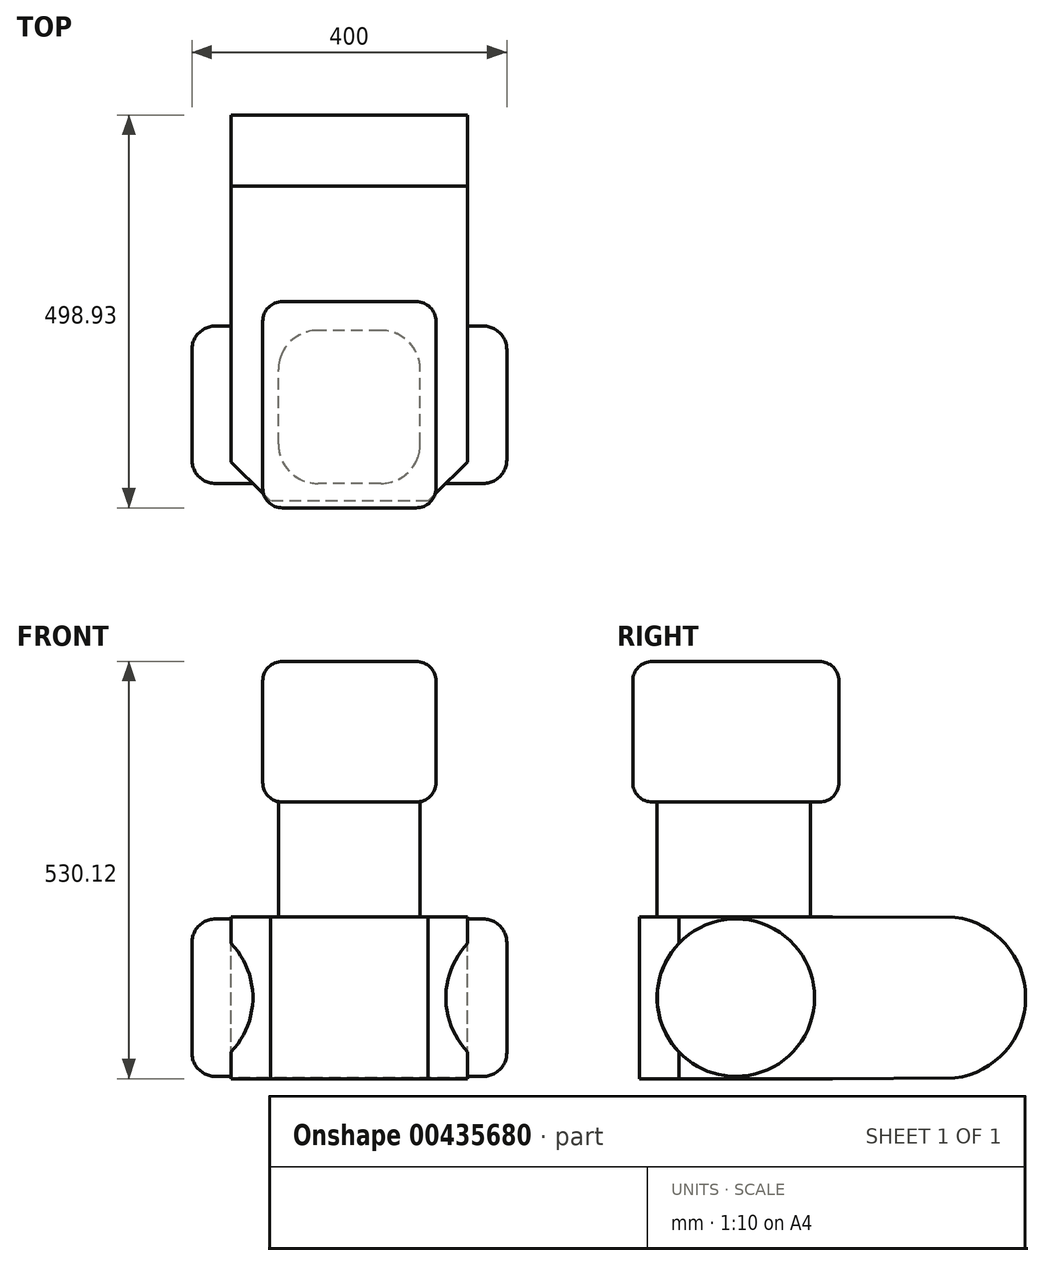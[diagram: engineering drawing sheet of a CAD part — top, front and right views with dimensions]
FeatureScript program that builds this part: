
annotation { "Feature Type Name" : "Feature", "Feature Type Description" : "" }
export const myFeature = defineFeature(function(context is Context, id is Id, definition is map)
    precondition{}
    {
        {
            var Q0;
            Q0=qCreatedBy(makeId("Right.planeOp"),FACE);
            var sketch = newSketch(context, id + "F0", { "sketchPlane" : qUnion([Q0])});
            skCircle(sketch, "E0", {"center": v(0, 0) * mm, "radius": 100 * mm});
            skLineSegment(sketch, "E1.bottom", {"start": v(-122.44, 102.88) * mm, "end": v(122.44, 102.88) * mm});
            skLineSegment(sketch, "E1.top", {"start": v(-122.44, -102.88) * mm, "end": v(122.44, -102.88) * mm});
            skLineSegment(sketch, "E1.left", {"start": v(-122.44, 102.88) * mm, "end": v(-122.44, -102.88) * mm});
            skLineSegment(sketch, "E1.right", {"start": v(122.44, 102.88) * mm, "end": v(122.44, -102.88) * mm});
            skPoint(sketch, "E2.firstSnap0", {"position": v(-122.44, 0) * mm});
            skLineSegment(sketch, "E2.bottom", {"start": v(-100, 0) * mm, "end": v(94.56, 0) * mm});
            skLineSegment(sketch, "E2.top", {"start": v(-100, 248.46) * mm, "end": v(94.56, 248.46) * mm});
            skLineSegment(sketch, "E2.left", {"start": v(-100, 0) * mm, "end": v(-100, 248.46) * mm});
            skLineSegment(sketch, "E2.right", {"start": v(94.56, 0) * mm, "end": v(94.56, 248.46) * mm});
            skLineSegment(sketch, "E3.bottom", {"start": v(130.98, 248.46) * mm, "end": v(-130.98, 248.46) * mm});
            skLineSegment(sketch, "E3.top", {"start": v(130.98, 427.24) * mm, "end": v(-130.98, 427.24) * mm});
            skLineSegment(sketch, "E3.left", {"start": v(130.98, 248.46) * mm, "end": v(130.98, 427.24) * mm});
            skLineSegment(sketch, "E3.right", {"start": v(-130.98, 248.46) * mm, "end": v(-130.98, 427.24) * mm});
            skPoint(sketch, "E3.middle", {"position": v(0, 337.85) * mm});
            skPoint(sketch, "E3.middle.positionSnap0", {"position": v(0, -102.88) * mm});
            skPoint(sketch, "E3.centerSnap0", {"position": v(0, -102.88) * mm});
            skCircle(sketch, "E4", {"center": v(265.07, 0) * mm, "radius": 102.88 * mm});
            skPoint(sketch, "E4.centerSnap0", {"position": v(122.44, 0) * mm});
            skLineSegment(sketch, "E5", {"start": v(122.44, 102.88) * mm, "end": v(277.99, 102.07) * mm});
            skLineSegment(sketch, "E6", {"start": v(277.99, 102.07) * mm, "end": v(277.99, -102.07) * mm});
            skLineSegment(sketch, "E7", {"start": v(277.99, -102.07) * mm, "end": v(122.44, -102.88) * mm});
            skLineSegment(sketch, "E8", {"start": v(-100, 210.38) * mm, "end": v(94.56, 209.37) * mm});
            skLineSegment(sketch, "E9", {"start": v(-100, 157.41) * mm, "end": v(94.56, 157.41) * mm});
            skLineSegment(sketch, "E10", {"start": v(-130.98, 296.46) * mm, "end": v(130.98, 296.46) * mm});
            skLineSegment(sketch, "E11", {"start": v(-130.98, 337.85) * mm, "end": v(130.98, 337.85) * mm});
            skLineSegment(sketch, "E12", {"start": v(-130.98, 385.86) * mm, "end": v(130.98, 385.86) * mm});
            skSolve(sketch);
        }
        {
            var Q0;
            {var subQ5=sQuery(id+"F0.wireOp",EDGE,"E9");Q0=makeQuery(id+"F0.imprint","IMPRINT",FACE,{"disambiguationData":[TD([[makeQuery(id+"F0.imprint","IMPRINT",EDGE,{"derivedFrom":subQ5}),-1.0]])]});}
            var Q1;
            {var subQ0=sQuery(id+"F0.wireOp",EDGE,"E8");Q1=makeQuery(id+"F0.imprint","IMPRINT",FACE,{"disambiguationData":[TD([[makeQuery(id+"F0.imprint","IMPRINT",EDGE,{"derivedFrom":subQ0}),-1.0]])]});}
            var Q2;
            {var subQ3=sQuery(id+"F0.wireOp",EDGE,"E8");Q2=makeQuery(id+"F0.imprint","IMPRINT",FACE,{"disambiguationData":[TD([[makeQuery(id+"F0.imprint","IMPRINT",EDGE,{"derivedFrom":subQ3}),1.0]])]});}
            extrude(context, id + "F1", {"entities" : qUnion([Q0, Q1, Q2]), "endBound" : BoundingType.SYMMETRIC, "depth" : 180 * mm});
        }
        {
            var Q0;
            {var subQ3=sQuery(id+"F0.wireOp",EDGE,"E10");Q0=makeQuery(id+"F0.imprint","IMPRINT",FACE,{"disambiguationData":[TD([[makeQuery(id+"F0.imprint","IMPRINT",EDGE,{"derivedFrom":subQ3}),-1.0]])]});}
            var Q1;
            {var subQ0=sQuery(id+"F0.wireOp",EDGE,"E10");Q1=makeQuery(id+"F0.imprint","IMPRINT",FACE,{"disambiguationData":[TD([[makeQuery(id+"F0.imprint","IMPRINT",EDGE,{"derivedFrom":subQ0}),1.0]])]});}
            var Q2;
            {var subQ0=sQuery(id+"F0.wireOp",EDGE,"E11");Q2=makeQuery(id+"F0.imprint","IMPRINT",FACE,{"disambiguationData":[TD([[makeQuery(id+"F0.imprint","IMPRINT",EDGE,{"derivedFrom":subQ0}),1.0]])]});}
            var Q3;
            {var subQ0=sQuery(id+"F0.wireOp",EDGE,"E3.top");Q3=makeQuery(id+"F0.imprint","IMPRINT",FACE,{"disambiguationData":[TD([[makeQuery(id+"F0.imprint","IMPRINT",EDGE,{"derivedFrom":subQ0}),1.0]])]});}
            extrude(context, id + "F2", {"entities" : qUnion([Q0, Q1, Q2, Q3]), "operationType" : NewBodyOperationType.ADD, "endBound" : BoundingType.SYMMETRIC, "depth" : 220 * mm});
        }
        {
            var Q0;
            Q0=makeQuery(id+"F0.imprint","IMPRINT",FACE,{"disambiguationData":[TD([[makeQuery(id+"F0.imprint","IMPRINT",EDGE,{"derivedFrom":sQuery(id+"F0.wireOp",EDGE,"E1.top")}),1.0]])]});
            var Q1;
            {var subQ0=sQuery(id+"F0.wireOp",EDGE,"E1.right");Q1=makeQuery(id+"F0.imprint","IMPRINT",FACE,{"disambiguationData":[TD([[makeQuery(id+"F0.imprint","IMPRINT",EDGE,{"derivedFrom":subQ0}),1.0]])]});}
            var Q2;
            {var subQ5=sQuery(id+"F0.wireOp",EDGE,"E6");Q2=makeQuery(id+"F0.imprint","IMPRINT",FACE,{"disambiguationData":[TD([[makeQuery(id+"F0.imprint","IMPRINT",EDGE,{"derivedFrom":subQ5}),-1.0]])]});}
            var Q3;
            {var subQ0=sQuery(id+"F0.wireOp",EDGE,"E6");Q3=makeQuery(id+"F0.imprint","IMPRINT",FACE,{"disambiguationData":[TD([[makeQuery(id+"F0.imprint","IMPRINT",EDGE,{"derivedFrom":subQ0}),1.0]])]});}
            var Q4;
            {var subQ0=sQuery(id+"F0.wireOp",EDGE,"E2.left");var subQ5=sQuery(id+"F0.wireOp",EDGE,"E1.bottom");var subQ6=makeQuery(id+"F0.imprint","INTERSECT",VERTEX,{"derivedFrom":[subQ5,subQ0]});Q4=makeQuery(id+"F0.imprint","IMPRINT",FACE,{"disambiguationData":[TD([[makeQuery(id+"F0.imprint","IMPRINT",EDGE,{"disambiguationData":[TD([[subQ6,-1.0]])],"derivedFrom":subQ5}),-1.0]])]});}
            extrude(context, id + "F3", {"entities" : qUnion([Q0, Q1, Q2, Q3, Q4]), "operationType" : NewBodyOperationType.ADD, "endBound" : BoundingType.SYMMETRIC, "depth" : 300 * mm});
        }
        {
            var Q0;
            {var subQ0=sQuery(id+"F0.wireOp",EDGE,"E2.bottom");Q0=makeQuery(id+"F0.imprint","IMPRINT",FACE,{"disambiguationData":[TD([[makeQuery(id+"F0.imprint","IMPRINT",EDGE,{"derivedFrom":subQ0}),1.0]])]});}
            var Q1;
            {var subQ0=sQuery(id+"F0.wireOp",EDGE,"E2.bottom");Q1=makeQuery(id+"F0.imprint","IMPRINT",FACE,{"disambiguationData":[TD([[makeQuery(id+"F0.imprint","IMPRINT",EDGE,{"derivedFrom":subQ0}),-1.0]])]});}
            extrude(context, id + "F4", {"entities" : qUnion([Q0, Q1]), "operationType" : NewBodyOperationType.ADD, "endBound" : BoundingType.SYMMETRIC, "depth" : 400 * mm});
        }
        {
            var Q0;
            Q0=makeQuery(id+"F2.opExtrude","SWEPT_EDGE",EDGE,{"disambiguationData":[OSD([sQuery(id+"F0.wireOp",EDGE,"E3.top"),sQuery(id+"F0.wireOp",EDGE,"E3.right")])]});
            var Q1;
            Q1=makeQuery(id+"F2.opExtrude","CAP_EDGE",EDGE,{"disambiguationData":[OSD([sQuery(id+"F0.wireOp",EDGE,"E3.top")])],"isStart":false});
            var Q2;
            Q2=makeQuery(id+"F2.opExtrude","SWEPT_EDGE",EDGE,{"disambiguationData":[OSD([sQuery(id+"F0.wireOp",EDGE,"E3.top"),sQuery(id+"F0.wireOp",EDGE,"E3.left")])]});
            var Q3;
            Q3=makeQuery(id+"F2.opExtrude","CAP_EDGE",EDGE,{"disambiguationData":[OSD([sQuery(id+"F0.wireOp",EDGE,"E3.top")])],"isStart":true});
            var Q4;
            Q4=makeQuery(id+"F2.opExtrude","CAP_EDGE",EDGE,{"disambiguationData":[OSD([sQuery(id+"F0.wireOp",EDGE,"E3.right")])],"isStart":false});
            var Q5;
            Q5=makeQuery(id+"F2.opExtrude","CAP_EDGE",EDGE,{"disambiguationData":[OSD([sQuery(id+"F0.wireOp",EDGE,"E3.bottom")])],"isStart":false});
            var Q6;
            Q6=makeQuery(id+"F2.opExtrude","CAP_FACE",FACE,{"disambiguationData":[OSD([sQuery(id+"F0.wireOp",EDGE,"E3.bottom"),sQuery(id+"F0.wireOp",EDGE,"E3.top"),sQuery(id+"F0.wireOp",EDGE,"E3.left"),sQuery(id+"F0.wireOp",EDGE,"E3.right")])],"isStart":false});
            var Q7;
            Q7=makeQuery(id+"F2.opExtrude","CAP_EDGE",EDGE,{"disambiguationData":[OSD([sQuery(id+"F0.wireOp",EDGE,"E3.right")])],"isStart":true});
            var Q8;
            Q8=makeQuery(id+"F2.opExtrude","SWEPT_EDGE",EDGE,{"disambiguationData":[OSD([sQuery(id+"F0.wireOp",EDGE,"E3.bottom"),sQuery(id+"F0.wireOp",EDGE,"E3.right")])]});
            var Q9;
            Q9=makeQuery(id+"F2.opExtrude","CAP_EDGE",EDGE,{"disambiguationData":[OSD([sQuery(id+"F0.wireOp",EDGE,"E3.bottom")])],"isStart":true});
            var Q10;
            Q10=makeQuery(id+"F2.opExtrude","CAP_EDGE",EDGE,{"disambiguationData":[OSD([sQuery(id+"F0.wireOp",EDGE,"E3.left")])],"isStart":true});
            var Q11;
            Q11=makeQuery(id+"F2.opExtrude","SWEPT_EDGE",EDGE,{"disambiguationData":[OSD([sQuery(id+"F0.wireOp",EDGE,"E3.bottom"),sQuery(id+"F0.wireOp",EDGE,"E3.left")])]});
            fillet(context, id + "F5", {"entities" : qUnion([Q0, Q1, Q2, Q3, Q4, Q5, Q6, Q7, Q8, Q9, Q10, Q11]), "radius" : 25 * mm, "tangentPropagation" : true, "allowEdgeOverflow" : false});
        }
        {
            var Q0;
            Q0=makeQuery(id+"F1.opExtrude","CAP_EDGE",EDGE,{"disambiguationData":[OSD([sQuery(id+"F0.wireOp",EDGE,"E2.left")])],"isStart":false});
            var Q1;
            Q1=makeQuery(id+"F1.opExtrude","CAP_EDGE",EDGE,{"disambiguationData":[OSD([sQuery(id+"F0.wireOp",EDGE,"E2.right")])],"isStart":false});
            var Q2;
            Q2=makeQuery(id+"F1.opExtrude","CAP_EDGE",EDGE,{"disambiguationData":[OSD([sQuery(id+"F0.wireOp",EDGE,"E2.right")])],"isStart":true});
            var Q3;
            Q3=makeQuery(id+"F1.opExtrude","CAP_EDGE",EDGE,{"disambiguationData":[OSD([sQuery(id+"F0.wireOp",EDGE,"E2.left")])],"isStart":true});
            fillet(context, id + "F6", {"entities" : qUnion([Q0, Q1, Q2, Q3]), "radius" : 50 * mm, "tangentPropagation" : true, "allowEdgeOverflow" : false});
        }
        {
            var Q0;
            Q0=makeQuery(id+"F4.opExtrude","CAP_EDGE",EDGE,{"disambiguationData":[OSD([sQuery(id+"F0.wireOp",EDGE,"E0")])],"isStart":false});
            var Q1;
            Q1=makeQuery(id+"F4.opExtrude","CAP_EDGE",EDGE,{"disambiguationData":[OSD([sQuery(id+"F0.wireOp",EDGE,"E0")])],"isStart":true});
            fillet(context, id + "F7", {"entities" : qUnion([Q0, Q1]), "radius" : 30 * mm, "tangentPropagation" : true, "allowEdgeOverflow" : false});
        }
        {
            var Q0;
            Q0=makeQuery(id+"F3.opExtrude","CAP_EDGE",EDGE,{"disambiguationData":[OSD([sQuery(id+"F0.wireOp",EDGE,"E1.left")])],"isStart":true});
            var Q1;
            Q1=makeQuery(id+"F3.opExtrude","CAP_EDGE",EDGE,{"disambiguationData":[OSD([sQuery(id+"F0.wireOp",EDGE,"E1.left")])],"isStart":false});
            chamfer(context, id + "F8", {"entities" : qUnion([Q0, Q1]), "width" : 50 * mm, "tangentPropagation" : true});
        }
    });
